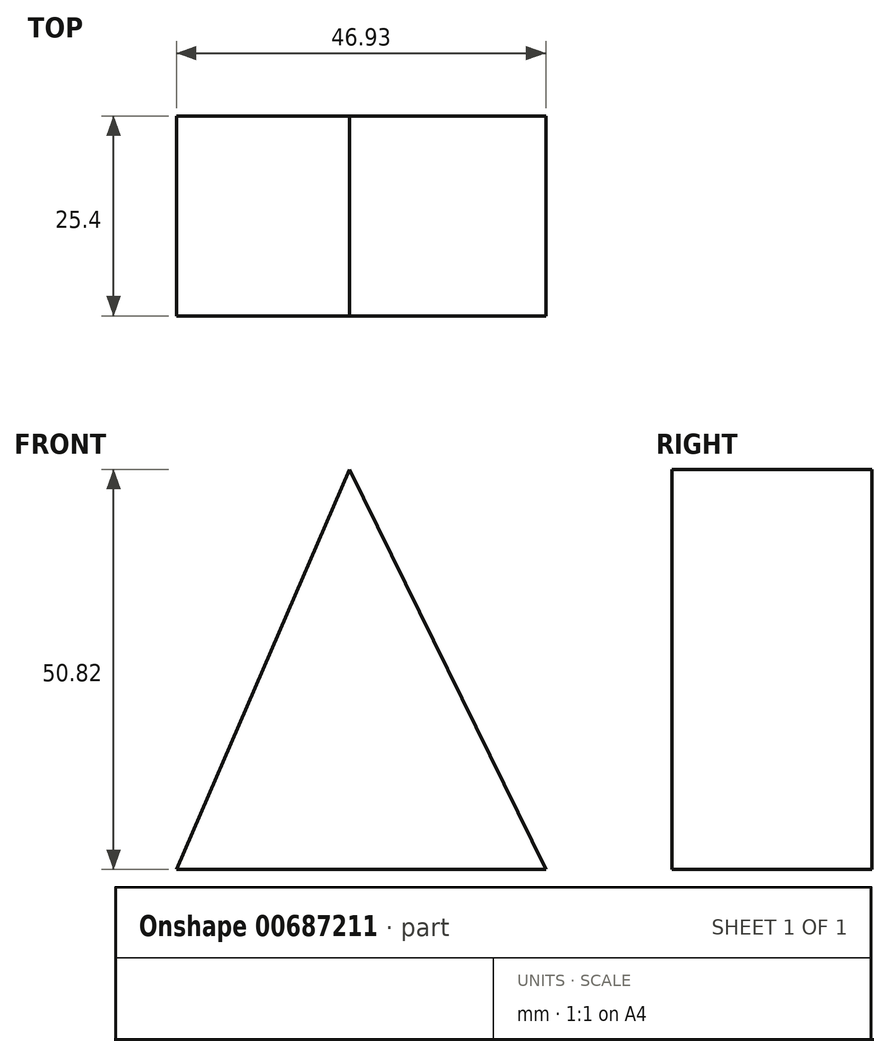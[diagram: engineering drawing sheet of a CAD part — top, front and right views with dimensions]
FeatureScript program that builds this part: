
annotation { "Feature Type Name" : "Feature", "Feature Type Description" : "" }
export const myFeature = defineFeature(function(context is Context, id is Id, definition is map)
    precondition{}
    {
        {
            var Q0;
            Q0=qCreatedBy(makeId("Front.planeOp"),FACE);
            var sketch = newSketch(context, id + "F0", { "sketchPlane" : qUnion([Q0])});
            skLineSegment(sketch, "E0", {"start": v(-21.98, 0) * mm, "end": v(0, 50.82) * mm});
            skLineSegment(sketch, "E1", {"start": v(0, 50.82) * mm, "end": v(24.95, 0) * mm});
            skLineSegment(sketch, "E2", {"start": v(-21.98, 0) * mm, "end": v(24.95, 0) * mm});
            skSolve(sketch);
        }
        {
            var Q0;
            Q0 = qSketchRegion(id + "F0", true);
            extrude(context, id + "F1", {"entities" : qUnion([Q0]), "depth" : 25.4 * mm, "offsetDistance" : 25.4 * mm});
        }
    });
